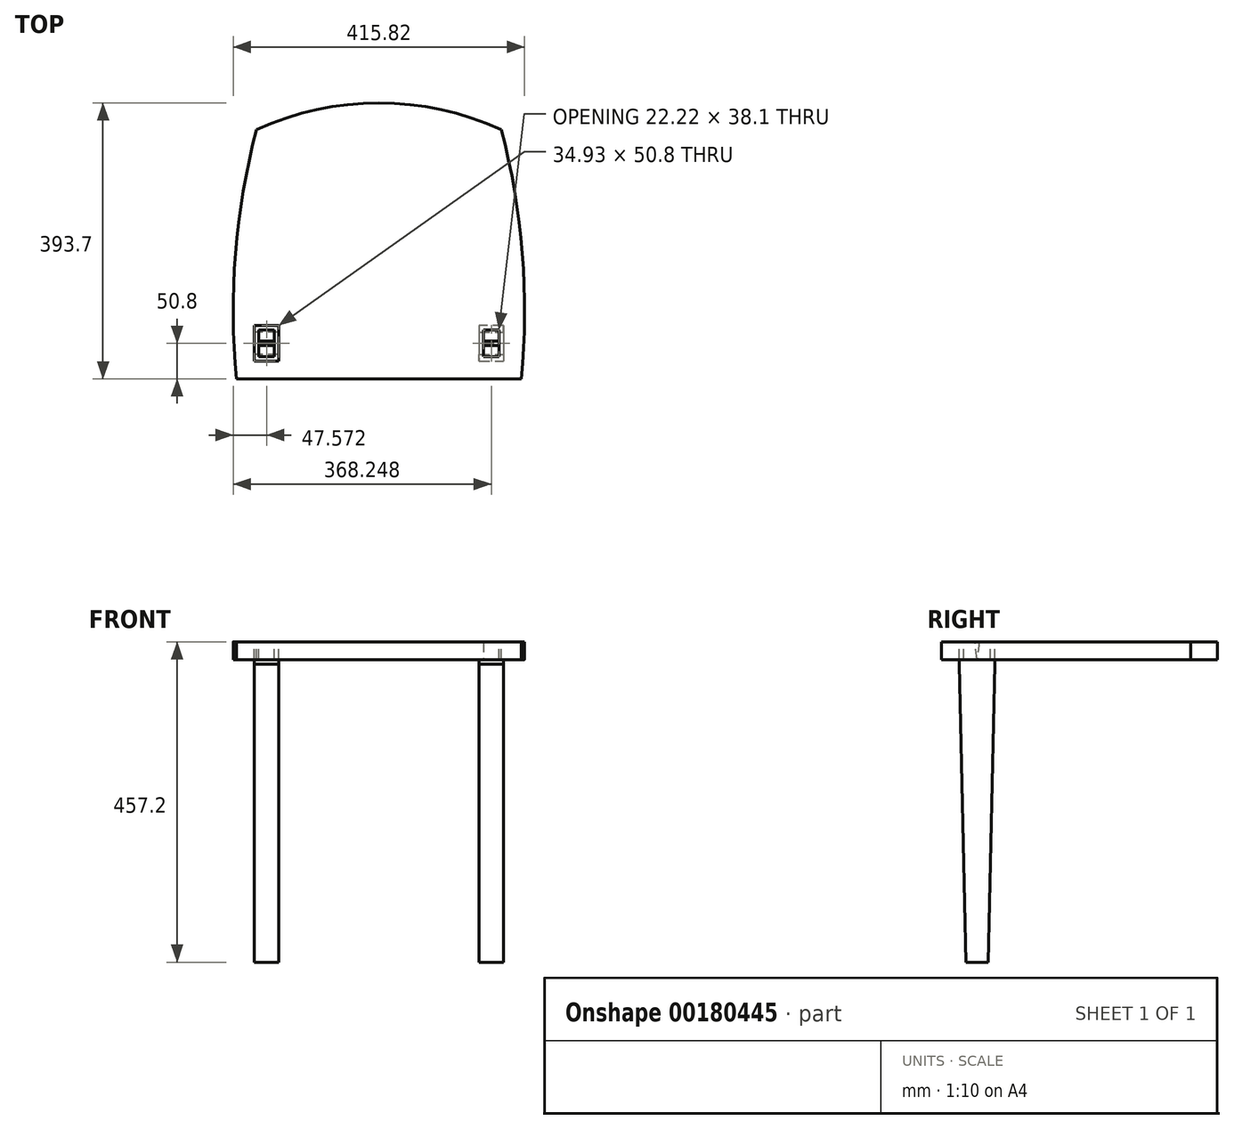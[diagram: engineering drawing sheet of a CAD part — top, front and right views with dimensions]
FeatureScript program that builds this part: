
annotation { "Feature Type Name" : "Feature", "Feature Type Description" : "" }
export const myFeature = defineFeature(function(context is Context, id is Id, definition is map)
    precondition{}
    {
        {
            var Q0;
            Q0=qCreatedBy(makeId("Top.planeOp"),FACE);
            var sketch = newSketch(context, id + "F0", { "sketchPlane" : qUnion([Q0])});
            skLineSegment(sketch, "E0", {"start": v(-203.2, -177.8) * mm, "end": v(203.2, -177.8) * mm});
            skLineSegment(sketch, "E1", {"start": v(203.2, -177.8) * mm, "end": v(174.62, 177.8) * mm, "construction": true});
            skLineSegment(sketch, "E2", {"start": v(174.63, 177.8) * mm, "end": v(-174.63, 177.8) * mm, "construction": true});
            skLineSegment(sketch, "E3", {"start": v(-174.63, 177.8) * mm, "end": v(-203.2, -177.8) * mm, "construction": true});
            skLineSegment(sketch, "E4", {"start": v(0, 0) * mm, "end": v(0, 177.8) * mm, "construction": true});
            skArc(sketch, "E5", {"start": v(174.63, 177.8) * mm, "mid": v(0, 215.9) * mm, "end": v(-174.63, 177.8) * mm});
            skArc(sketch, "E6", {"start": v(-174.63, 177.8) * mm, "mid": v(-204.64, 1.26) * mm, "end": v(-203.2, -177.8) * mm});
            skArc(sketch, "E7", {"start": v(203.2, -177.8) * mm, "mid": v(204.64, 1.26) * mm, "end": v(174.63, 177.8) * mm});
            skSolve(sketch);
        }
        {
            var Q0;
            Q0 = qSketchRegion(id + "F0", true);
            extrude(context, id + "F1", {"entities" : qUnion([Q0]), "oppositeDirection" : true, "depth" : 25.4 * mm});
        }
        {
            var Q0;
            Q0=qCreatedBy(makeId("Top.planeOp"),FACE);
            var sketch = newSketch(context, id + "F2", { "sketchPlane" : qUnion([Q0])});
            skLineSegment(sketch, "E8.bottom", {"start": v(-177.8, -101.6) * mm, "end": v(-142.88, -101.6) * mm});
            skLineSegment(sketch, "E8.top", {"start": v(-177.8, -152.4) * mm, "end": v(-142.88, -152.4) * mm});
            skLineSegment(sketch, "E8.left", {"start": v(-177.8, -101.6) * mm, "end": v(-177.8, -152.4) * mm});
            skLineSegment(sketch, "E8.right", {"start": v(-142.88, -101.6) * mm, "end": v(-142.88, -152.4) * mm});
            skSolve(sketch);
        }
        {
            var Q0;
            Q0 = qSketchRegion(id + "F2", true);
            extrude(context, id + "F3", {"entities" : qUnion([Q0]), "oppositeDirection" : true, "depth" : 457.2 * mm});
        }
        {
            var Q0;
            Q0=makeQuery(id+"F3.opExtrude","CAP_FACE",FACE,{"disambiguationData":[OSD([sQuery(id+"F2.wireOp",EDGE,"E8.bottom"),sQuery(id+"F2.wireOp",EDGE,"E8.top"),sQuery(id+"F2.wireOp",EDGE,"E8.left"),sQuery(id+"F2.wireOp",EDGE,"E8.right")])],"isStart":true});
            var sketch = newSketch(context, id + "F4", { "sketchPlane" : qUnion([Q0])});
            skLineSegment(sketch, "E9.bottom", {"start": v(-171.45, -107.95) * mm, "end": v(-149.23, -107.95) * mm});
            skLineSegment(sketch, "E9.top", {"start": v(-171.45, -146.05) * mm, "end": v(-149.23, -146.05) * mm});
            skLineSegment(sketch, "E9.left", {"start": v(-171.45, -107.95) * mm, "end": v(-171.45, -146.05) * mm});
            skLineSegment(sketch, "E9.right", {"start": v(-149.23, -107.95) * mm, "end": v(-149.23, -146.05) * mm});
            skLineSegment(sketch, "E10.0", {"start": v(-177.8, -101.6) * mm, "end": v(-177.8, -152.4) * mm});
            skLineSegment(sketch, "E11.0", {"start": v(-177.8, -101.6) * mm, "end": v(-142.88, -101.6) * mm});
            skLineSegment(sketch, "E12.0", {"start": v(-142.88, -101.6) * mm, "end": v(-142.88, -152.4) * mm});
            skLineSegment(sketch, "E12.1", {"start": v(-177.8, -152.4) * mm, "end": v(-142.88, -152.4) * mm});
            skSolve(sketch);
        }
        {
            var Q0;
            Q0 = qSketchRegion(id + "F4", true);
            extrude(context, id + "F5", {"entities" : qUnion([Q0]), "operationType" : NewBodyOperationType.REMOVE, "oppositeDirection" : true, "depth" : 25.4 * mm});
        }
        {
            var Q0;
            Q0=makeQuery(id+"F5.boolean.opBoolean","COPY",FACE,{"derivedFrom":makeQuery(id+"F5.opExtrude","SWEPT_FACE",FACE,{"disambiguationData":[OSD([sQuery(id+"F4.wireOp",EDGE,"E9.left")])]})});
            var sketch = newSketch(context, id + "F6", { "sketchPlane" : qUnion([Q0])});
            skLineSegment(sketch, "E13", {"start": v(127, 0) * mm, "end": v(127, -25.4) * mm, "construction": true});
            skLineSegment(sketch, "E14", {"start": v(127, -25.4) * mm, "end": v(123.83, 0) * mm});
            skLineSegment(sketch, "E15", {"start": v(123.83, 0) * mm, "end": v(130.17, 0) * mm});
            skLineSegment(sketch, "E16", {"start": v(130.17, 0) * mm, "end": v(127, -25.4) * mm});
            skSolve(sketch);
        }
        {
            var Q0;
            Q0 = qSketchRegion(id + "F6", true);
            var Q1;
            Q1=makeQuery(id+"F5.boolean.opBoolean","COPY",FACE,{"derivedFrom":makeQuery(id+"F5.opExtrude","SWEPT_FACE",FACE,{"disambiguationData":[OSD([sQuery(id+"F4.wireOp",EDGE,"E9.right")])]})});
            extrude(context, id + "F7", {"entities" : qUnion([Q0]), "operationType" : NewBodyOperationType.REMOVE, "endBound" : BoundingType.UP_TO_SURFACE, "oppositeDirection" : true, "endBoundEntityFace" : qUnion([Q1]), "depth" : 25.4 * mm});
        }
        {
            var Q0;
            Q0 = qSketchRegion(id + "F6", true);
            var Q1;
            {var subQ0=sQuery(id+"F4.wireOp",EDGE,"E9.top");var subQ1=sQuery(id+"F4.wireOp",EDGE,"E9.right");var subQ2=makeQuery(id+"F5.boolean.opBoolean","COPY",FACE,{"derivedFrom":makeQuery(id+"F5.opExtrude","SWEPT_FACE",FACE,{"disambiguationData":[OSD([subQ1])]})});Q1=makeQuery(id+"F7.boolean.opBoolean","SPLIT",FACE,{"disambiguationData":[TD([makeQuery(id+"F5.boolean.opBoolean","COPY",FACE,{"derivedFrom":makeQuery(id+"F5.opExtrude","SWEPT_FACE",FACE,{"disambiguationData":[OSD([subQ0])]})})])],"derivedFrom":subQ2});}
            extrude(context, id + "F8", {"entities" : qUnion([Q0]), "endBound" : BoundingType.UP_TO_SURFACE, "oppositeDirection" : true, "endBoundEntityFace" : qUnion([Q1]), "depth" : 25.4 * mm});
        }
        {
            var Q0;
            Q0=makeQuery(id+"F3.opExtrude","SWEPT_FACE",FACE,{"disambiguationData":[OSD([sQuery(id+"F2.wireOp",EDGE,"E8.left")])]});
            var sketch = newSketch(context, id + "F9", { "sketchPlane" : qUnion([Q0])});
            skLineSegment(sketch, "E17", {"start": v(142.88, -457.2) * mm, "end": v(152.4, -31.75) * mm});
            skLineSegment(sketch, "E18", {"start": v(111.13, -457.2) * mm, "end": v(101.6, -31.75) * mm});
            skLineSegment(sketch, "E19.0", {"start": v(152.4, -457.2) * mm, "end": v(152.4, -31.75) * mm});
            skLineSegment(sketch, "E19.1", {"start": v(101.6, -457.2) * mm, "end": v(111.12, -457.2) * mm});
            skLineSegment(sketch, "E19.2", {"start": v(101.6, -457.2) * mm, "end": v(101.6, -31.75) * mm});
            skPoint(sketch, "E20.orphan", {"position": v(101.6, -25.4) * mm});
            skPoint(sketch, "E21.orphan", {"position": v(152.4, -25.4) * mm});
            skLineSegment(sketch, "E22.trimOffspring", {"start": v(142.88, -457.2) * mm, "end": v(152.4, -457.2) * mm});
            skSolve(sketch);
        }
        {
            var Q0;
            Q0 = qSketchRegion(id + "F9", true);
            var Q1;
            Q1=makeQuery(id+"F3.opExtrude","SWEPT_FACE",FACE,{"disambiguationData":[OSD([sQuery(id+"F2.wireOp",EDGE,"E8.right")])]});
            extrude(context, id + "F10", {"entities" : qUnion([Q0]), "operationType" : NewBodyOperationType.REMOVE, "endBound" : BoundingType.UP_TO_SURFACE, "oppositeDirection" : true, "endBoundEntityFace" : qUnion([Q1]), "depth" : 25.4 * mm});
        }
        {
            var Q0;
            Q0=makeQuery(id+"F8.opExtrude","SWEPT_BODY",BODY,{"disambiguationData":[OSD([sQuery(id+"F6.wireOp",EDGE,"E14"),sQuery(id+"F6.wireOp",EDGE,"E15"),sQuery(id+"F6.wireOp",EDGE,"E16")])]});
            var Q1;
            Q1=makeQuery(id+"F3.opExtrude","SWEPT_BODY",BODY,{"disambiguationData":[OSD([sQuery(id+"F2.wireOp",EDGE,"E8.bottom"),sQuery(id+"F2.wireOp",EDGE,"E8.top"),sQuery(id+"F2.wireOp",EDGE,"E8.left"),sQuery(id+"F2.wireOp",EDGE,"E8.right")])]});
            var Q2;
            Q2=qCreatedBy(makeId("Right.planeOp"),FACE);
            mirror(context, id + "F11", {"entities" : qUnion([Q0, Q1]), "mirrorPlane" : qUnion([Q2])});
        }
        {
            var Q0;
            Q0=makeQuery(id+"F3.opExtrude","SWEPT_BODY",BODY,{"disambiguationData":[OSD([sQuery(id+"F2.wireOp",EDGE,"E8.bottom"),sQuery(id+"F2.wireOp",EDGE,"E8.top"),sQuery(id+"F2.wireOp",EDGE,"E8.left"),sQuery(id+"F2.wireOp",EDGE,"E8.right")])]});
            var Q1;
            Q1=makeQuery(id+"F11.opPattern","COPY",BODY,{"derivedFrom":makeQuery(id+"F3.opExtrude","SWEPT_BODY",BODY,{"disambiguationData":[OSD([sQuery(id+"F2.wireOp",EDGE,"E8.bottom"),sQuery(id+"F2.wireOp",EDGE,"E8.top"),sQuery(id+"F2.wireOp",EDGE,"E8.left"),sQuery(id+"F2.wireOp",EDGE,"E8.right")])]}),"instanceName":"1"});
            var Q2;
            Q2=makeQuery(id+"F8.opExtrude","SWEPT_BODY",BODY,{"disambiguationData":[OSD([sQuery(id+"F6.wireOp",EDGE,"E14"),sQuery(id+"F6.wireOp",EDGE,"E15"),sQuery(id+"F6.wireOp",EDGE,"E16")])]});
            var Q3;
            Q3=makeQuery(id+"F11.opPattern","COPY",BODY,{"derivedFrom":makeQuery(id+"F8.opExtrude","SWEPT_BODY",BODY,{"disambiguationData":[OSD([sQuery(id+"F6.wireOp",EDGE,"E14"),sQuery(id+"F6.wireOp",EDGE,"E15"),sQuery(id+"F6.wireOp",EDGE,"E16")])]}),"instanceName":"1"});
            var Q4;
            Q4=makeQuery(id+"F1.opExtrude","SWEPT_BODY",BODY,{"disambiguationData":[OSD([sQuery(id+"F0.wireOp",EDGE,"E0"),sQuery(id+"F0.wireOp",EDGE,"E5"),sQuery(id+"F0.wireOp",EDGE,"E6"),sQuery(id+"F0.wireOp",EDGE,"E7")])]});
            booleanBodies(context, id + "F12", {"operationType" : BooleanOperationType.SUBTRACTION, "tools" : qUnion([Q0, Q1, Q2, Q3]), "targets" : qUnion([Q4]), "keepTools" : true});
        }
        {
            var Q0;
            Q0=makeQuery(id+"F0.imprint","IMPRINT",FACE,{"disambiguationData":[TD([[makeQuery(id+"F0.imprint","IMPRINT",EDGE,{"derivedFrom":sQuery(id+"F0.wireOp",EDGE,"E0")}),1.0]])]});
            var sketch = newSketch(context, id + "F13", { "sketchPlane" : qUnion([Q0])});
            skLineSegment(sketch, "E23", {"start": v(117.63, 132.4) * mm, "end": v(139.35, 192.06) * mm});
            skLineSegment(sketch, "E24", {"start": v(139.35, 192.06) * mm, "end": v(163.21, 183.38) * mm});
            skPoint(sketch, "E25", {"position": v(134.16, 177.8) * mm});
            skSolve(sketch);
        }
        {
            var Q0;
            Q0=sQuery(id+"F13.wireOp",EDGE,"E23");
            cPlane(context, id + "F14", {"entities" : qUnion([Q0]), "cplaneType" : CPlaneType.LINE_ANGLE, "offset" : 25.4 * mm, "angle" : 90 * degree, "width" : 152.4 * mm, "height" : 152.4 * mm});
        }
    });
